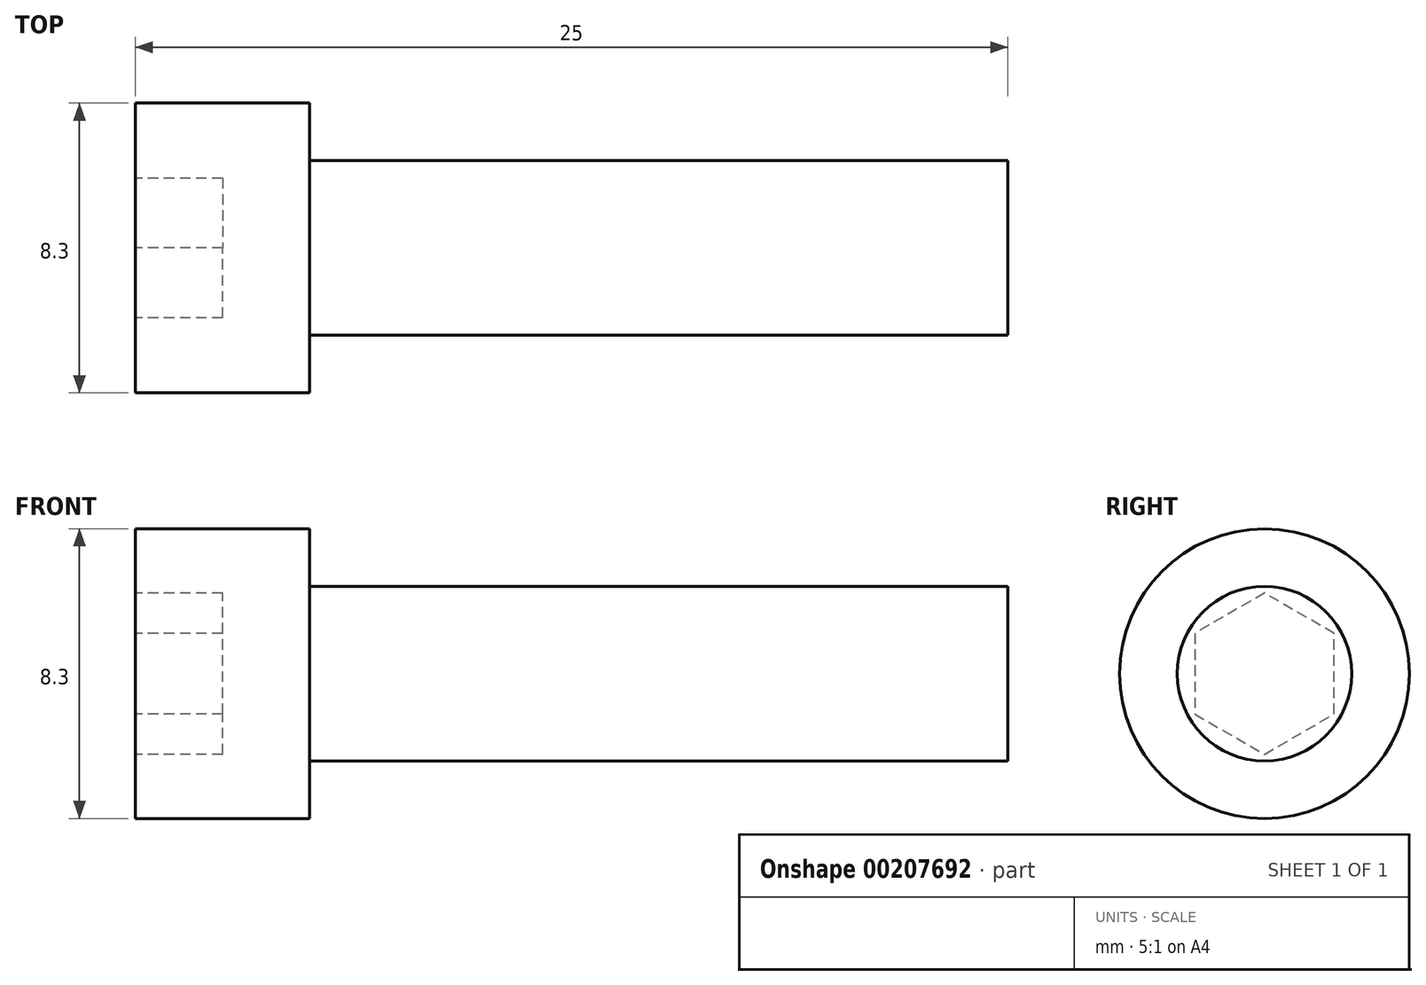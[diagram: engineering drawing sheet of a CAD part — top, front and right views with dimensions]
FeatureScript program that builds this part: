
annotation { "Feature Type Name" : "Feature", "Feature Type Description" : "" }
export const myFeature = defineFeature(function(context is Context, id is Id, definition is map)
    precondition{}
    {
        {
            var Q0;
            Q0=qCreatedBy(makeId("Front.planeOp"),FACE);
            var sketch = newSketch(context, id + "F0", { "sketchPlane" : qUnion([Q0])});
            skLineSegment(sketch, "E0.bottom", {"start": v(0, 2.5) * mm, "end": v(20, 2.5) * mm});
            skLineSegment(sketch, "E0.top", {"start": v(0, 0) * mm, "end": v(20, 0) * mm});
            skLineSegment(sketch, "E0.left", {"start": v(0, 2.5) * mm, "end": v(0, 0) * mm});
            skLineSegment(sketch, "E0.right", {"start": v(20, 2.5) * mm, "end": v(20, 0) * mm});
            skLineSegment(sketch, "E1.bottom", {"start": v(-5, 4.15) * mm, "end": v(0, 4.15) * mm});
            skLineSegment(sketch, "E1.top", {"start": v(-5, 0) * mm, "end": v(0, 0) * mm});
            skLineSegment(sketch, "E1.left", {"start": v(-5, 4.15) * mm, "end": v(-5, 0) * mm});
            skLineSegment(sketch, "E1.right", {"start": v(0, 4.15) * mm, "end": v(0, 0) * mm});
            skSolve(sketch);
        }
        {
            var Q0;
            Q0=qSketchRegion(id+"F0",true);
            var Q1;
            Q1=sQuery(id+"F0.wireOp",EDGE,"E0.top");
            revolve(context, id + "F1", {"entities" : qUnion([Q0]), "axis" : qUnion([Q1]), "revolveType" : RevolveType.FULL});
        }
        {
            var Q0;
            Q0=makeQuery(id+"F1.opRevolve","SWEPT_FACE",FACE,{"disambiguationData":[OSD([sQuery(id+"F0.wireOp",EDGE,"E1.left")])]});
            var sketch = newSketch(context, id + "F2", { "sketchPlane" : qUnion([Q0])});
            skCircle(sketch, "E2.cCircle", {"center": v(0, 0) * mm, "radius": 2 * mm, "construction": true});
            skLineSegment(sketch, "E2.0", {"start": v(-2, 1.15) * mm, "end": v(0, 2.3) * mm});
            skLineSegment(sketch, "E2.1", {"start": v(0, 2.3) * mm, "end": v(2, 1.15) * mm});
            skLineSegment(sketch, "E2.2", {"start": v(2, 1.15) * mm, "end": v(2, -1.15) * mm});
            skLineSegment(sketch, "E2.3", {"start": v(2, -1.15) * mm, "end": v(0, -2.3) * mm});
            skLineSegment(sketch, "E2.4", {"start": v(0, -2.3) * mm, "end": v(-2, -1.15) * mm});
            skLineSegment(sketch, "E2.5", {"start": v(-2, -1.15) * mm, "end": v(-2, 1.15) * mm});
            skPoint(sketch, "E2.0.midPoint", {"position": v(-1, 1.73) * mm});
            skSolve(sketch);
        }
        {
            var Q0;
            Q0=qSketchRegion(id+"F2",true);
            extrude(context, id + "F3", {"entities" : qUnion([Q0]), "operationType" : NewBodyOperationType.REMOVE, "oppositeDirection" : true, "depth" : 2.5 * mm});
        }
    });
